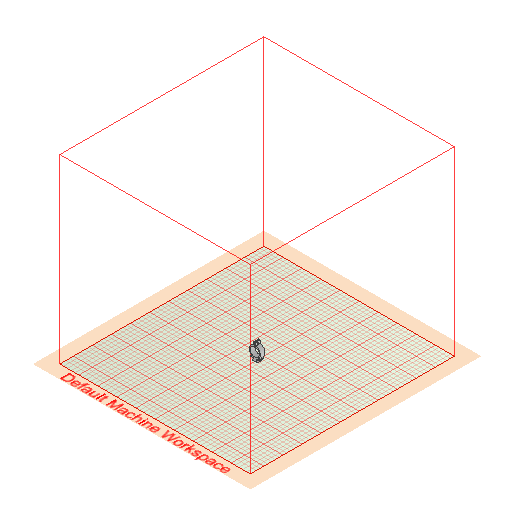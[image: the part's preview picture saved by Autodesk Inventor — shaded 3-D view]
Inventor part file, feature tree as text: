
AUTODESK INVENTOR PART (.ipt)
format: ipt  version: 2022 (Build 260153000, 153)  size: 337,408 bytes
history: native  units: mm
features: extrude x3, sketch x3, projected_geometry x3, plane x1
ambient origin geometry x8: Origin, YZ Plane, XZ Plane, XY Plane, X Axis, Y Axis, Z Axis, Center Point
bodies: Solid1 (feature_tree)
feature tree (10):
  extrude  "Extrusion1"  Depth=8.0mm
  plane  "Work Plane1"
  extrude  "Extrusion2"  Depth=2.0mm
  extrude  "Extrusion3"  Depth=2.0mm
  sketch  "Sketch1"  dims[d0=8.0mm d1=12.0mm]
  sketch  "Sketch2"  dims[d3=3.0mm d5=2.0mm]
  projected_geometry  "Projected Loop1"
  projected_geometry  "Projected Loop2"
  sketch  "Sketch3"  dims[d6=10.0mm d7=0.0mm d8=2.0mm d9=25.0mm d10=0.0mm d11=5.0mm d12=5.0mm d13=2.0mm d14=9.0mm d15=20.0mm d16=13.0mm d17=1.0mm d18=1.5mm d19=1.5mm d20=10.0mm d21=0.0mm d22=3.0mm d24=10.0mm d25=0.0mm d26=0.5mm d27=19.0mm d28=4.0mm]
  projected_geometry  "Projected Loop3"
